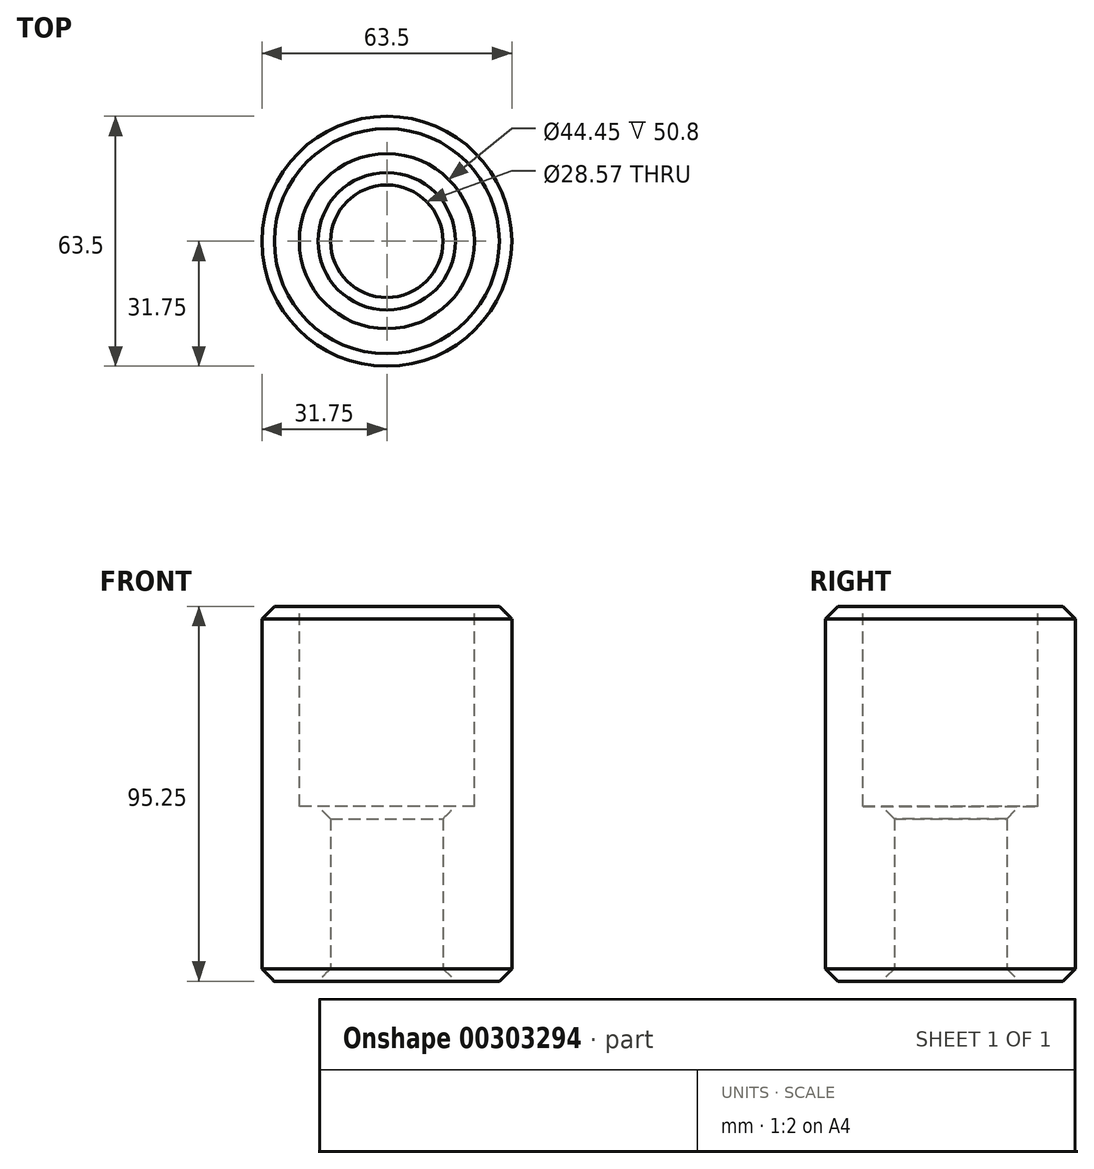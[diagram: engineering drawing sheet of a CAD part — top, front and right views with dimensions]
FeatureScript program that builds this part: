
annotation { "Feature Type Name" : "Feature", "Feature Type Description" : "" }
export const myFeature = defineFeature(function(context is Context, id is Id, definition is map)
    precondition{}
    {
        {
            var Q0;
            Q0=qCreatedBy(makeId("Front.planeOp"),FACE);
            var sketch = newSketch(context, id + "F0", { "sketchPlane" : qUnion([Q0])});
            skLineSegment(sketch, "E0", {"start": v(0, 0) * mm, "end": v(0, 60.78) * mm, "construction": true});
            skLineSegment(sketch, "E1", {"start": v(0, 0) * mm, "end": v(31.75, 0) * mm});
            skLineSegment(sketch, "E2", {"start": v(31.75, 0) * mm, "end": v(31.75, 95.25) * mm});
            skLineSegment(sketch, "E3", {"start": v(31.75, 95.25) * mm, "end": v(0, 95.25) * mm});
            skLineSegment(sketch, "E4", {"start": v(0, 95.25) * mm, "end": v(0, 0) * mm});
            skSolve(sketch);
        }
        {
            var Q0;
            Q0=makeQuery(id+"F0.imprint","IMPRINT",FACE,{"disambiguationData":[TD([[makeQuery(id+"F0.imprint","IMPRINT",EDGE,{"derivedFrom":sQuery(id+"F0.wireOp",EDGE,"E1")}),1.0]])]});
            var Q1;
            Q1=sQuery(id+"F0.wireOp",EDGE,"E0");
            revolve(context, id + "F1", {"entities" : qUnion([Q0]), "axis" : qUnion([Q1]), "revolveType" : RevolveType.FULL});
        }
        {
            var Q0;
            Q0=makeQuery(id+"F1.opRevolve","SWEPT_FACE",FACE,{"disambiguationData":[OSD([sQuery(id+"F0.wireOp",EDGE,"E3")])]});
            var sketch = newSketch(context, id + "F2", { "sketchPlane" : qUnion([Q0])});
            skCircle(sketch, "E5", {"center": v(0, 0) * mm, "radius": 22.23 * mm});
            skSolve(sketch);
        }
        {
            var Q0;
            Q0 = qSketchRegion(id + "F2", true);
            extrude(context, id + "F3", {"entities" : qUnion([Q0]), "operationType" : NewBodyOperationType.REMOVE, "oppositeDirection" : true, "depth" : 50.8 * mm});
        }
        {
            var Q0;
            Q0=makeQuery(id+"F1.opRevolve","SWEPT_FACE",FACE,{"disambiguationData":[OSD([sQuery(id+"F0.wireOp",EDGE,"E1")])]});
            var sketch = newSketch(context, id + "F4", { "sketchPlane" : qUnion([Q0])});
            skCircle(sketch, "E6", {"center": v(0, 0) * mm, "radius": 14.29 * mm});
            skSolve(sketch);
        }
        {
            var Q0;
            Q0=makeQuery(id+"F4.imprint","IMPRINT",FACE,{"disambiguationData":[TD([[makeQuery(id+"F4.imprint","IMPRINT",EDGE,{"derivedFrom":sQuery(id+"F4.wireOp",EDGE,"E6")}),1.0]])]});
            extrude(context, id + "F5", {"entities" : qUnion([Q0]), "operationType" : NewBodyOperationType.REMOVE, "endBound" : BoundingType.THROUGH_ALL, "oppositeDirection" : true, "depth" : 25.4 * mm});
        }
        {
            var Q0;
            Q0=makeQuery(id+"F1.opRevolve","SWEPT_EDGE",EDGE,{"disambiguationData":[OSD([sQuery(id+"F0.wireOp",EDGE,"E1"),sQuery(id+"F0.wireOp",EDGE,"E2")])]});
            var Q1;
            Q1=makeQuery(id+"F1.opRevolve","SWEPT_EDGE",EDGE,{"disambiguationData":[OSD([sQuery(id+"F0.wireOp",EDGE,"E2"),sQuery(id+"F0.wireOp",EDGE,"E3")])]});
            var Q2;
            Q2=makeQuery(id+"F3.boolean.opBoolean","COPY",EDGE,{"derivedFrom":makeQuery(id+"F3.opExtrude","CAP_EDGE",EDGE,{"disambiguationData":[OSD([sQuery(id+"F2.wireOp",EDGE,"E5")])],"isStart":true})});
            var Q3;
            Q3=makeQuery(id+"F5.boolean.opBoolean","INTERSECT",EDGE,{"derivedFrom":[makeQuery(id+"F3.boolean.opBoolean","COPY",FACE,{"derivedFrom":makeQuery(id+"F3.opExtrude","CAP_FACE",FACE,{"disambiguationData":[OSD([sQuery(id+"F2.wireOp",EDGE,"E5")])],"isStart":false})}),makeQuery(id+"F5.opExtrude","SWEPT_FACE",FACE,{"disambiguationData":[OSD([sQuery(id+"F4.wireOp",EDGE,"E6")])]})]});
            var Q4;
            Q4=makeQuery(id+"F5.boolean.opBoolean","COPY",FACE,{"derivedFrom":makeQuery(id+"F5.opExtrude","SWEPT_FACE",FACE,{"disambiguationData":[OSD([sQuery(id+"F4.wireOp",EDGE,"E6")])]})});
            chamfer(context, id + "F6", {"entities" : qUnion([Q0, Q1, Q2, Q3, Q4]), "width" : 3.17 * mm, "tangentPropagation" : true});
        }
    });
